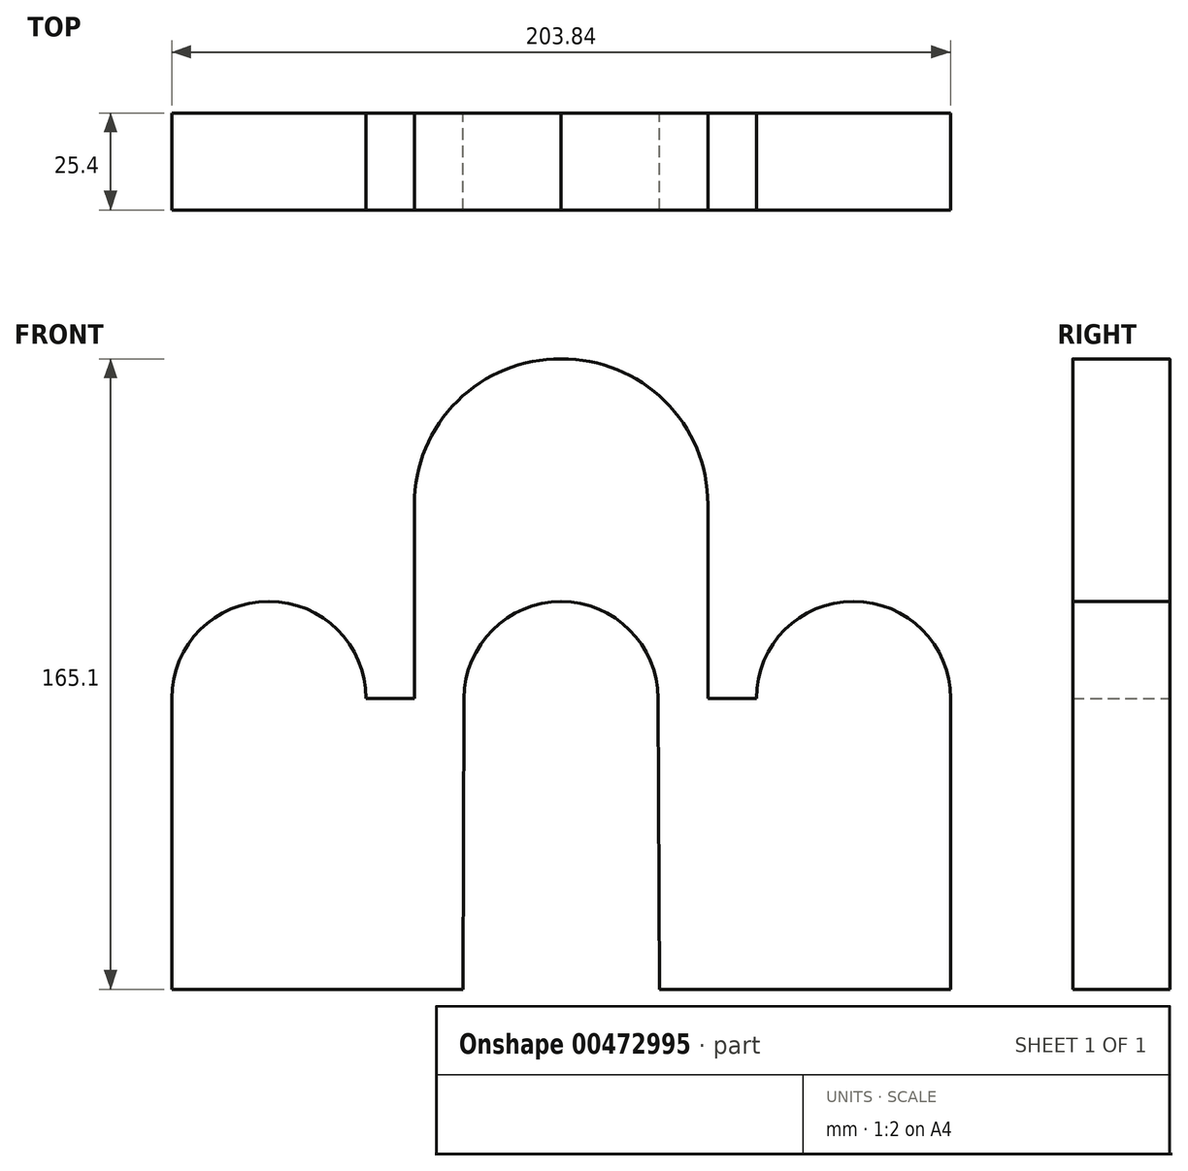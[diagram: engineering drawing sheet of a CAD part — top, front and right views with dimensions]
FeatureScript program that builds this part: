
annotation { "Feature Type Name" : "Feature", "Feature Type Description" : "" }
export const myFeature = defineFeature(function(context is Context, id is Id, definition is map)
    precondition{}
    {
        {
            var Q0;
            Q0=qCreatedBy(makeId("Front.planeOp"),FACE);
            var sketch = newSketch(context, id + "F0", { "sketchPlane" : qUnion([Q0])});
            skLineSegment(sketch, "E0", {"start": v(0, 0) * mm, "end": v(0, 76.2) * mm});
            skLineSegment(sketch, "E1", {"start": v(0, 0) * mm, "end": v(76.2, 0) * mm});
            skLineSegment(sketch, "E2", {"start": v(76.2, 0) * mm, "end": v(76.52, 76.2) * mm});
            skArc(sketch, "E3", {"start": v(0, 76.2) * mm, "mid": v(25.4, 101.6) * mm, "end": v(50.8, 76.2) * mm});
            skLineSegment(sketch, "E4", {"start": v(0, 76.2) * mm, "end": v(50.8, 76.2) * mm, "construction": true});
            skArc(sketch, "E5", {"start": v(76.52, 76.2) * mm, "mid": v(84, 94.1) * mm, "end": v(101.92, 101.5) * mm});
            skLineSegment(sketch, "E6", {"start": v(101.92, 76.1) * mm, "end": v(101.92, 101.5) * mm, "construction": true});
            skLineSegment(sketch, "E7", {"start": v(101.92, 88.8) * mm, "end": v(101.92, 93.36) * mm, "construction": true});
            skLineSegment(sketch, "E8", {"start": v(50.8, 76.2) * mm, "end": v(63.5, 76.2) * mm});
            skLineSegment(sketch, "E9", {"start": v(63.5, 76.2) * mm, "end": v(63.5, 127) * mm});
            skArc(sketch, "E10", {"start": v(63.5, 127) * mm, "mid": v(74.77, 154.05) * mm, "end": v(101.92, 165.1) * mm});
            skPoint(sketch, "E10.endSnap0", {"position": v(101.92, 91.08) * mm});
            skArc(sketch, "E11.MirrorCS", {"start": v(140.34, 127) * mm, "mid": v(129.07, 154.05) * mm, "end": v(101.92, 165.1) * mm});
            skLineSegment(sketch, "E12.MirrorCS", {"start": v(140.34, 76.2) * mm, "end": v(140.34, 127) * mm});
            skLineSegment(sketch, "E13.MirrorCS", {"start": v(153.04, 76.2) * mm, "end": v(140.34, 76.2) * mm});
            skArc(sketch, "E14.MirrorCS", {"start": v(203.84, 76.2) * mm, "mid": v(178.44, 101.6) * mm, "end": v(153.04, 76.2) * mm});
            skLineSegment(sketch, "E15.MirrorCS", {"start": v(203.84, 0) * mm, "end": v(203.84, 76.2) * mm});
            skLineSegment(sketch, "E16.MirrorCS", {"start": v(203.84, 0) * mm, "end": v(127.64, 0) * mm});
            skLineSegment(sketch, "E17.MirrorCS", {"start": v(127.64, 0) * mm, "end": v(127.32, 76.2) * mm});
            skArc(sketch, "E18.MirrorCS", {"start": v(127.32, 76.2) * mm, "mid": v(119.84, 94.1) * mm, "end": v(101.92, 101.5) * mm});
            skSolve(sketch);
        }
        {
            var Q0;
            Q0 = qSketchRegion(id + "F0", true);
            extrude(context, id + "F1", {"entities" : qUnion([Q0]), "depth" : 25.4 * mm});
        }
    });
